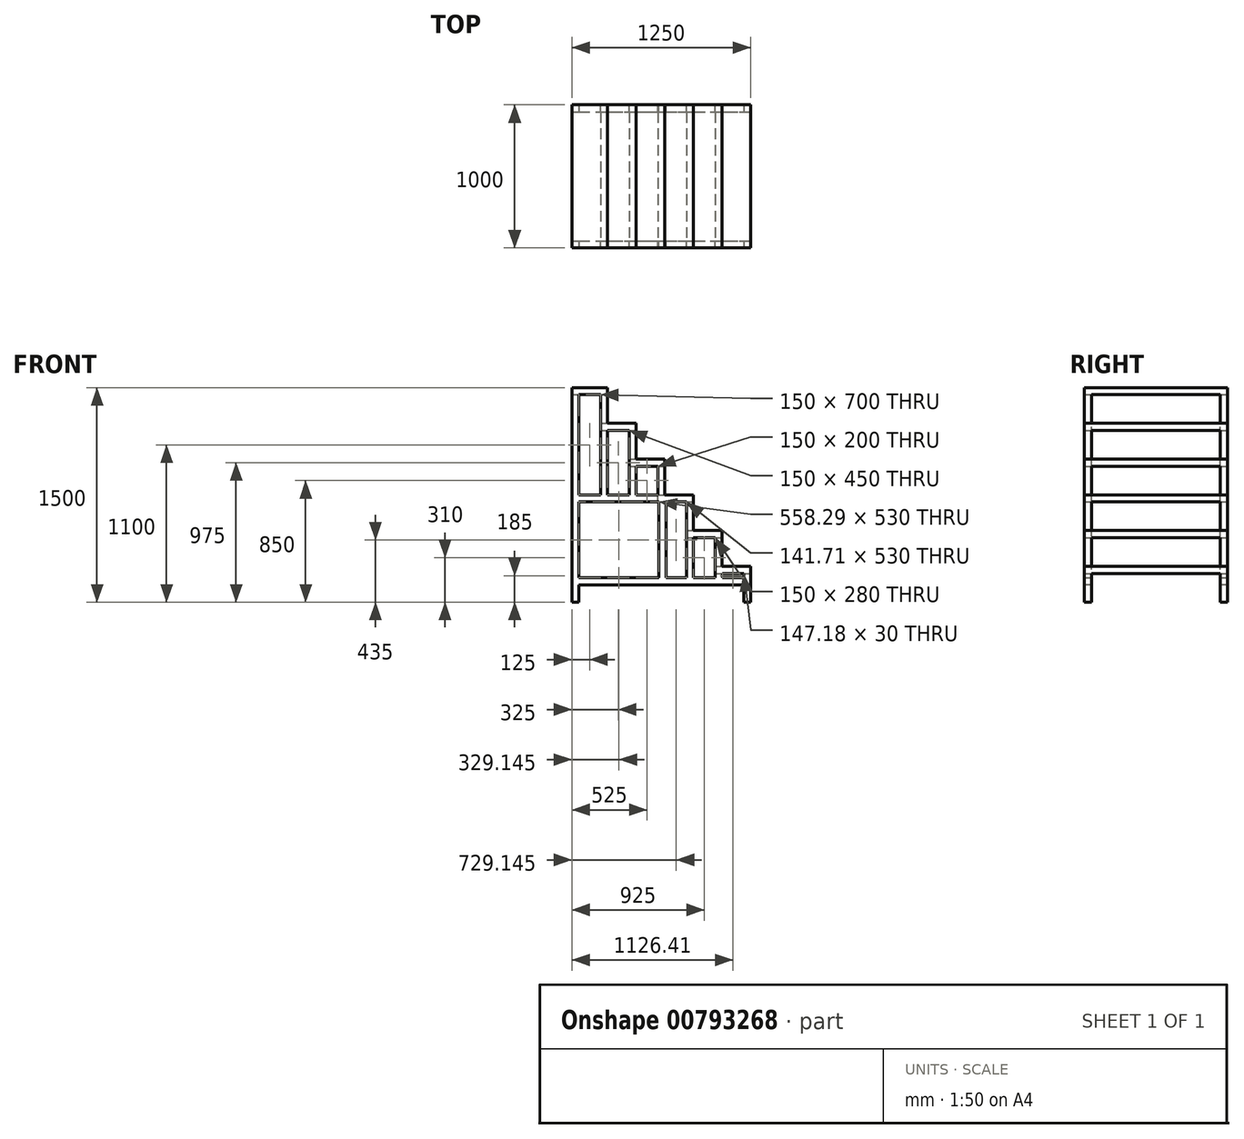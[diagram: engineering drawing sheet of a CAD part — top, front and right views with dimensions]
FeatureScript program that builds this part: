
annotation { "Feature Type Name" : "Feature", "Feature Type Description" : "" }
export const myFeature = defineFeature(function(context is Context, id is Id, definition is map)
    precondition{}
    {
        {
            var Q0;
            Q0=qCreatedBy(makeId("Front.planeOp"),FACE);
            var sketch = newSketch(context, id + "F0", { "sketchPlane" : qUnion([Q0])});
            skLineSegment(sketch, "E0.bottom", {"start": v(0, 0) * mm, "end": v(1250, 0) * mm});
            skLineSegment(sketch, "E0.top", {"start": v(0, 250) * mm, "end": v(1250, 250) * mm});
            skLineSegment(sketch, "E0.left", {"start": v(0, 0) * mm, "end": v(0, 250) * mm});
            skLineSegment(sketch, "E0.right", {"start": v(1250, 0) * mm, "end": v(1250, 250) * mm});
            skLineSegment(sketch, "E1.bottom", {"start": v(0, 250) * mm, "end": v(1050, 250) * mm});
            skLineSegment(sketch, "E1.top", {"start": v(0, 500) * mm, "end": v(1050, 500) * mm});
            skLineSegment(sketch, "E1.left", {"start": v(0, 250) * mm, "end": v(0, 500) * mm});
            skLineSegment(sketch, "E1.right", {"start": v(1050, 250) * mm, "end": v(1050, 500) * mm});
            skLineSegment(sketch, "E2.bottom", {"start": v(0, 500) * mm, "end": v(850, 500) * mm});
            skLineSegment(sketch, "E2.top", {"start": v(0, 750) * mm, "end": v(850, 750) * mm});
            skLineSegment(sketch, "E2.left", {"start": v(0, 500) * mm, "end": v(0, 750) * mm});
            skLineSegment(sketch, "E2.right", {"start": v(850, 500) * mm, "end": v(850, 750) * mm});
            skLineSegment(sketch, "E3.bottom", {"start": v(0, 750) * mm, "end": v(650, 750) * mm});
            skLineSegment(sketch, "E3.top", {"start": v(0, 1000) * mm, "end": v(650, 1000) * mm});
            skLineSegment(sketch, "E3.left", {"start": v(0, 750) * mm, "end": v(0, 1000) * mm});
            skLineSegment(sketch, "E3.right", {"start": v(650, 750) * mm, "end": v(650, 1000) * mm});
            skLineSegment(sketch, "E4.bottom", {"start": v(0, 1000) * mm, "end": v(450, 1000) * mm});
            skLineSegment(sketch, "E4.top", {"start": v(0, 1250) * mm, "end": v(450, 1250) * mm});
            skLineSegment(sketch, "E4.left", {"start": v(0, 1000) * mm, "end": v(0, 1250) * mm});
            skLineSegment(sketch, "E4.right", {"start": v(450, 1000) * mm, "end": v(450, 1250) * mm});
            skLineSegment(sketch, "E5.bottom", {"start": v(0, 1250) * mm, "end": v(250, 1250) * mm});
            skLineSegment(sketch, "E5.top", {"start": v(0, 1500) * mm, "end": v(250, 1500) * mm});
            skLineSegment(sketch, "E5.left", {"start": v(0, 1250) * mm, "end": v(0, 1500) * mm});
            skLineSegment(sketch, "E5.right", {"start": v(250, 1250) * mm, "end": v(250, 1500) * mm});
            skSolve(sketch);
        }
        {
            var Q0;
            Q0=qSketchRegion(id+"F0",true);
            extrude(context, id + "F1", {"entities" : qUnion([Q0]), "depth" : 1000 * mm, "offsetDistance" : 25 * mm});
        }
        {
            var Q0;
            Q0=makeQuery(id+"F1.opExtrude","SWEPT_FACE",FACE,{"disambiguationData":[OSD([sQuery(id+"F0.wireOp",EDGE,"E0.left"),sQuery(id+"F0.wireOp",EDGE,"E1.left"),sQuery(id+"F0.wireOp",EDGE,"E2.left"),sQuery(id+"F0.wireOp",EDGE,"E3.left"),sQuery(id+"F0.wireOp",EDGE,"E4.left"),sQuery(id+"F0.wireOp",EDGE,"E5.left")])]});
            shell(context, id + "F2", {"entities" : qUnion([Q0]), "thickness" : 50 * mm});
        }
        {
            var Q0;
            Q0=makeQuery(id+"F1.opExtrude","CAP_FACE",FACE,{"disambiguationData":[OSD([sQuery(id+"F0.wireOp",EDGE,"E0.bottom"),sQuery(id+"F0.wireOp",EDGE,"E0.top"),sQuery(id+"F0.wireOp",EDGE,"E0.left"),sQuery(id+"F0.wireOp",EDGE,"E0.right"),sQuery(id+"F0.wireOp",EDGE,"E1.top"),sQuery(id+"F0.wireOp",EDGE,"E1.left"),sQuery(id+"F0.wireOp",EDGE,"E1.right"),sQuery(id+"F0.wireOp",EDGE,"E2.top"),sQuery(id+"F0.wireOp",EDGE,"E2.left"),sQuery(id+"F0.wireOp",EDGE,"E2.right"),sQuery(id+"F0.wireOp",EDGE,"E3.top"),sQuery(id+"F0.wireOp",EDGE,"E3.left"),sQuery(id+"F0.wireOp",EDGE,"E3.right"),sQuery(id+"F0.wireOp",EDGE,"E4.top"),sQuery(id+"F0.wireOp",EDGE,"E4.left"),sQuery(id+"F0.wireOp",EDGE,"E4.right"),sQuery(id+"F0.wireOp",EDGE,"E5.top"),sQuery(id+"F0.wireOp",EDGE,"E5.left"),sQuery(id+"F0.wireOp",EDGE,"E5.right")])],"isStart":false});
            var sketch = newSketch(context, id + "F3", { "sketchPlane" : qUnion([Q0])});
            skLineSegment(sketch, "E6.bottom", {"start": v(50, 0) * mm, "end": v(1200, 0) * mm});
            skLineSegment(sketch, "E6.top", {"start": v(50, 120) * mm, "end": v(1200, 120) * mm});
            skLineSegment(sketch, "E6.left", {"start": v(50, 0) * mm, "end": v(50, 120) * mm});
            skLineSegment(sketch, "E6.right", {"start": v(1200, 0) * mm, "end": v(1200, 120) * mm});
            skSolve(sketch);
        }
        {
            var Q0;
            Q0=makeQuery(id+"F3.imprint","IMPRINT",FACE,{"disambiguationData":[TD([[makeQuery(id+"F3.imprint","IMPRINT",EDGE,{"derivedFrom":sQuery(id+"F3.wireOp",EDGE,"E6.bottom")}),1.0]])]});
            extrude(context, id + "F4", {"entities" : qUnion([Q0]), "operationType" : NewBodyOperationType.REMOVE, "oppositeDirection" : true, "depth" : 1100 * mm, "offsetDistance" : 25 * mm});
        }
        {
            var Q0;
            Q0=makeQuery(id+"F1.opExtrude","SWEPT_FACE",FACE,{"disambiguationData":[OSD([sQuery(id+"F0.wireOp",EDGE,"E0.right")])]});
            var sketch = newSketch(context, id + "F5", { "sketchPlane" : qUnion([Q0])});
            skLineSegment(sketch, "E7.bottom", {"start": v(-950, 0) * mm, "end": v(-50, 0) * mm});
            skLineSegment(sketch, "E7.top", {"start": v(-950, 200) * mm, "end": v(-50, 200) * mm});
            skLineSegment(sketch, "E7.left", {"start": v(-950, 0) * mm, "end": v(-950, 200) * mm});
            skLineSegment(sketch, "E7.right", {"start": v(-50, 0) * mm, "end": v(-50, 200) * mm});
            skSolve(sketch);
        }
        {
            var Q0;
            Q0=qSketchRegion(id+"F5",true);
            extrude(context, id + "F6", {"entities" : qUnion([Q0]), "operationType" : NewBodyOperationType.REMOVE, "oppositeDirection" : true, "depth" : 5000 * mm, "offsetDistance" : 25 * mm});
        }
        {
            var Q0;
            Q0=makeQuery(id+"F1.opExtrude","SWEPT_FACE",FACE,{"disambiguationData":[OSD([sQuery(id+"F0.wireOp",EDGE,"E1.right")])]});
            var sketch = newSketch(context, id + "F7", { "sketchPlane" : qUnion([Q0])});
            skLineSegment(sketch, "E8.bottom", {"start": v(-950, 250) * mm, "end": v(-50, 250) * mm});
            skLineSegment(sketch, "E8.top", {"start": v(-950, 450) * mm, "end": v(-50, 450) * mm});
            skLineSegment(sketch, "E8.left", {"start": v(-950, 250) * mm, "end": v(-950, 450) * mm});
            skLineSegment(sketch, "E8.right", {"start": v(-50, 250) * mm, "end": v(-50, 450) * mm});
            skSolve(sketch);
        }
        {
            var Q0;
            Q0=qSketchRegion(id+"F7",true);
            extrude(context, id + "F8", {"entities" : qUnion([Q0]), "operationType" : NewBodyOperationType.REMOVE, "oppositeDirection" : true, "depth" : 300 * mm, "offsetDistance" : 25 * mm});
        }
        {
            var Q0;
            Q0=makeQuery(id+"F1.opExtrude","SWEPT_FACE",FACE,{"disambiguationData":[OSD([sQuery(id+"F0.wireOp",EDGE,"E2.right")])]});
            var sketch = newSketch(context, id + "F9", { "sketchPlane" : qUnion([Q0])});
            skLineSegment(sketch, "E9.bottom", {"start": v(-950, 500) * mm, "end": v(-50, 500) * mm});
            skLineSegment(sketch, "E9.top", {"start": v(-950, 700) * mm, "end": v(-50, 700) * mm});
            skLineSegment(sketch, "E9.left", {"start": v(-950, 500) * mm, "end": v(-950, 700) * mm});
            skLineSegment(sketch, "E9.right", {"start": v(-50, 500) * mm, "end": v(-50, 700) * mm});
            skSolve(sketch);
        }
        {
            var Q0;
            Q0=qSketchRegion(id+"F9",true);
            extrude(context, id + "F10", {"entities" : qUnion([Q0]), "operationType" : NewBodyOperationType.REMOVE, "oppositeDirection" : true, "depth" : 300 * mm, "offsetDistance" : 25 * mm});
        }
        {
            var Q0;
            Q0=makeQuery(id+"F1.opExtrude","SWEPT_FACE",FACE,{"disambiguationData":[OSD([sQuery(id+"F0.wireOp",EDGE,"E3.right")])]});
            var sketch = newSketch(context, id + "F11", { "sketchPlane" : qUnion([Q0])});
            skLineSegment(sketch, "E10.bottom", {"start": v(-950, 750) * mm, "end": v(-50, 750) * mm});
            skLineSegment(sketch, "E10.top", {"start": v(-950, 950) * mm, "end": v(-50, 950) * mm});
            skLineSegment(sketch, "E10.left", {"start": v(-950, 750) * mm, "end": v(-950, 950) * mm});
            skLineSegment(sketch, "E10.right", {"start": v(-50, 750) * mm, "end": v(-50, 950) * mm});
            skSolve(sketch);
        }
        {
            var Q0;
            Q0=qSketchRegion(id+"F11",true);
            extrude(context, id + "F12", {"entities" : qUnion([Q0]), "operationType" : NewBodyOperationType.REMOVE, "oppositeDirection" : true, "depth" : 300 * mm, "offsetDistance" : 25 * mm});
        }
        {
            var Q0;
            Q0=makeQuery(id+"F1.opExtrude","SWEPT_FACE",FACE,{"disambiguationData":[OSD([sQuery(id+"F0.wireOp",EDGE,"E4.right")])]});
            var sketch = newSketch(context, id + "F13", { "sketchPlane" : qUnion([Q0])});
            skLineSegment(sketch, "E11.bottom", {"start": v(-950, 1000) * mm, "end": v(-50, 1000) * mm});
            skLineSegment(sketch, "E11.top", {"start": v(-950, 1200) * mm, "end": v(-50, 1200) * mm});
            skLineSegment(sketch, "E11.left", {"start": v(-950, 1000) * mm, "end": v(-950, 1200) * mm});
            skLineSegment(sketch, "E11.right", {"start": v(-50, 1000) * mm, "end": v(-50, 1200) * mm});
            skSolve(sketch);
        }
        {
            var Q0;
            Q0=qSketchRegion(id+"F13",true);
            extrude(context, id + "F14", {"entities" : qUnion([Q0]), "operationType" : NewBodyOperationType.REMOVE, "oppositeDirection" : true, "depth" : 300 * mm, "offsetDistance" : 25 * mm});
        }
        {
            var Q0;
            Q0=makeQuery(id+"F1.opExtrude","SWEPT_FACE",FACE,{"disambiguationData":[OSD([sQuery(id+"F0.wireOp",EDGE,"E5.right")])]});
            var sketch = newSketch(context, id + "F15", { "sketchPlane" : qUnion([Q0])});
            skLineSegment(sketch, "E12.bottom", {"start": v(-950, 1250) * mm, "end": v(-50, 1250) * mm});
            skLineSegment(sketch, "E12.top", {"start": v(-950, 1450) * mm, "end": v(-50, 1450) * mm});
            skLineSegment(sketch, "E12.left", {"start": v(-950, 1250) * mm, "end": v(-950, 1450) * mm});
            skLineSegment(sketch, "E12.right", {"start": v(-50, 1250) * mm, "end": v(-50, 1450) * mm});
            skSolve(sketch);
        }
        {
            var Q0;
            Q0=qSketchRegion(id+"F15",true);
            extrude(context, id + "F16", {"entities" : qUnion([Q0]), "operationType" : NewBodyOperationType.REMOVE, "oppositeDirection" : true, "depth" : 300 * mm, "offsetDistance" : 25 * mm});
        }
        {
            var Q0;
            Q0=makeQuery(id+"F1.opExtrude","CAP_FACE",FACE,{"disambiguationData":[OSD([sQuery(id+"F0.wireOp",EDGE,"E0.bottom"),sQuery(id+"F0.wireOp",EDGE,"E0.top"),sQuery(id+"F0.wireOp",EDGE,"E0.left"),sQuery(id+"F0.wireOp",EDGE,"E0.right"),sQuery(id+"F0.wireOp",EDGE,"E1.top"),sQuery(id+"F0.wireOp",EDGE,"E1.left"),sQuery(id+"F0.wireOp",EDGE,"E1.right"),sQuery(id+"F0.wireOp",EDGE,"E2.top"),sQuery(id+"F0.wireOp",EDGE,"E2.left"),sQuery(id+"F0.wireOp",EDGE,"E2.right"),sQuery(id+"F0.wireOp",EDGE,"E3.top"),sQuery(id+"F0.wireOp",EDGE,"E3.left"),sQuery(id+"F0.wireOp",EDGE,"E3.right"),sQuery(id+"F0.wireOp",EDGE,"E4.top"),sQuery(id+"F0.wireOp",EDGE,"E4.left"),sQuery(id+"F0.wireOp",EDGE,"E4.right"),sQuery(id+"F0.wireOp",EDGE,"E5.top"),sQuery(id+"F0.wireOp",EDGE,"E5.left"),sQuery(id+"F0.wireOp",EDGE,"E5.right")])],"isStart":true});
            var sketch = newSketch(context, id + "F17", { "sketchPlane" : qUnion([Q0])});
            skLineSegment(sketch, "E13", {"start": v(-600, 750) * mm, "end": v(-450, 750) * mm});
            skLineSegment(sketch, "E14", {"start": v(-50, 750) * mm, "end": v(-50, 1450) * mm});
            skLineSegment(sketch, "E15", {"start": v(-50, 1450) * mm, "end": v(-200, 1450) * mm});
            skLineSegment(sketch, "E16", {"start": v(-200, 1450) * mm, "end": v(-200, 1200) * mm});
            skLineSegment(sketch, "E17", {"start": v(-250, 1200) * mm, "end": v(-400, 1200) * mm});
            skLineSegment(sketch, "E18", {"start": v(-400, 1200) * mm, "end": v(-400, 950) * mm});
            skLineSegment(sketch, "E19", {"start": v(-450, 950) * mm, "end": v(-600, 950) * mm});
            skLineSegment(sketch, "E20", {"start": v(-600, 950) * mm, "end": v(-600, 750) * mm});
            skLineSegment(sketch, "E21", {"start": v(-608.29, 700) * mm, "end": v(-50, 700) * mm});
            skLineSegment(sketch, "E22", {"start": v(-400, 950) * mm, "end": v(-400, 750) * mm});
            skLineSegment(sketch, "E23", {"start": v(-450, 950) * mm, "end": v(-450, 750) * mm});
            skLineSegment(sketch, "E24", {"start": v(-200, 1200) * mm, "end": v(-200, 750) * mm});
            skLineSegment(sketch, "E25", {"start": v(-250, 1200) * mm, "end": v(-250, 750) * mm});
            skLineSegment(sketch, "E26", {"start": v(-800, 700) * mm, "end": v(-800, 450) * mm});
            skLineSegment(sketch, "E27", {"start": v(-850, 450) * mm, "end": v(-1000, 450) * mm});
            skLineSegment(sketch, "E28", {"start": v(-1000, 450) * mm, "end": v(-1000, 200) * mm});
            skLineSegment(sketch, "E29", {"start": v(-1052.82, 200) * mm, "end": v(-1200, 200) * mm});
            skLineSegment(sketch, "E30", {"start": v(-1200, 200) * mm, "end": v(-1200, 170) * mm});
            skLineSegment(sketch, "E31", {"start": v(-1200, 170) * mm, "end": v(-1052.82, 170) * mm});
            skLineSegment(sketch, "E32", {"start": v(-50, 170) * mm, "end": v(-50, 700) * mm});
            skLineSegment(sketch, "E33", {"start": v(-658.29, 700) * mm, "end": v(-658.29, 170) * mm});
            skLineSegment(sketch, "E34", {"start": v(-608.29, 700) * mm, "end": v(-608.29, 170) * mm});
            skLineSegment(sketch, "E35", {"start": v(-800, 450) * mm, "end": v(-800, 170) * mm});
            skLineSegment(sketch, "E36", {"start": v(-850, 450) * mm, "end": v(-850, 170) * mm});
            skLineSegment(sketch, "E37", {"start": v(-1000, 200) * mm, "end": v(-1000, 170) * mm});
            skLineSegment(sketch, "E38", {"start": v(-1052.82, 200) * mm, "end": v(-1052.82, 170) * mm});
            skLineSegment(sketch, "E39", {"start": v(-800, 700) * mm, "end": v(-658.29, 700) * mm});
            skPoint(sketch, "E40.orphan", {"position": v(0, 700) * mm});
            skPoint(sketch, "E41.orphan", {"position": v(0, 750) * mm});
            skLineSegment(sketch, "E42.trimOffspring", {"start": v(-200, 750) * mm, "end": v(-50, 750) * mm});
            skLineSegment(sketch, "E43.trimOffspring", {"start": v(-400, 750) * mm, "end": v(-250, 750) * mm});
            skLineSegment(sketch, "E44.trimOffspring", {"start": v(-608.29, 170) * mm, "end": v(-50, 170) * mm});
            skLineSegment(sketch, "E45.trimOffspring", {"start": v(-800, 170) * mm, "end": v(-658.29, 170) * mm});
            skLineSegment(sketch, "E46.trimOffspring", {"start": v(-1000, 170) * mm, "end": v(-850, 170) * mm});
            skSolve(sketch);
        }
        {
            var Q0;
            Q0=qSketchRegion(id+"F17",true);
            extrude(context, id + "F18", {"entities" : qUnion([Q0]), "operationType" : NewBodyOperationType.REMOVE, "oppositeDirection" : true, "depth" : 5000 * mm, "offsetDistance" : 25 * mm});
        }
    });
